# Revit family: Panel CARA
name_source: partatom
category: Mechanical Equipment
revit_build: Autodesk Revit 2016 (Build: 20150220_1215(x64)
units: mm (PartAtom-declared; Revit-internal decimal feet)

## family parameters
Cut with Voids When Loaded = No
Host = Face
Part Type = Normal
Room Calculation Point = No
Round Connector Dimension = Use Diameter
Shared = No

## types (2) — shared parameters
Altura colector = 85 mm  [stored 0.278871 ft]
Anchura colector = 624 mm  [stored 2.04724 ft]
Autor = 6d ingenieros
CPC Material = Bosch_CPC
Certificados = Marcado CE de conformidad, Solar Keymark
Conector colectorl (DN) = 15 mm  [stored 0.0492126 ft]
Contenido abosorbedor (Vfi) = 0.85 l
Longitud colector = 1947 mm  [stored 6.3878 ft]
Manufacturer = BOSCH
Peso neto = 18 kg
PlasticArea = Bosch_160-160-160
Presión servicio admisible = 10 bar
Str = Bosch_Str
Sup. general colector (Agr) = 1,22 m2
Tube = Bosch_TubePanel
URL = www.buderus.es/buderus/grupo-bosch.html
Versión = 1.0
zero-valued in all types: Default Elevation

## per-type parameters (varying)
| type | CPC | Coef. cuadrático transmisión térmica (a2) | Coef. lineal transmisión térmica (a1) | Description | Factor correc. ángulo inclinación (IAM) | Grado efec. colector ΔT = 40 K ( ŋcal) | Inclinación permitida | Max. potencia calorífica (Pmax) a 1000 W/m2 | Model | Rendimiento óptico (ŋo) | Sup. abosorbedor (Aab) | Área de apertura (Aap) |
| VK120-2 Montaje tejado-fachada | No | 0.015 W(m2K2) | 2.99 W/(m2K) | Captador solar de tubos de vacío sin espejos reflectores de alto rendimiento, modelo VK120-2 | 1,27 | 64 % | 0 - 90º | 362 W | VK120-2 | 0.787 | 0,39 m2 | 0.46 m2 |
| VK120-2 CPC Montaje tejado-fachada | Yes | 0.012 W/(m2K2) | 0.782 W(m2K) | Captador solar de tubos de vacío con espejos reflectores de alto rendimiento, modelo VK120-2 CPC | 1 | 61 % | 25 - 90º | 650 W | VK120-2 CPC | 0.663 | 1.07 m2 | 0.98 m2 |

note: [stored X ft] marks values corroborated as IEEE doubles in the binary element streams (Revit-internal decimal feet)

## geometry (parser evidence)
native form markers: Sweep x1
no freeform markers — native parametric forms only
